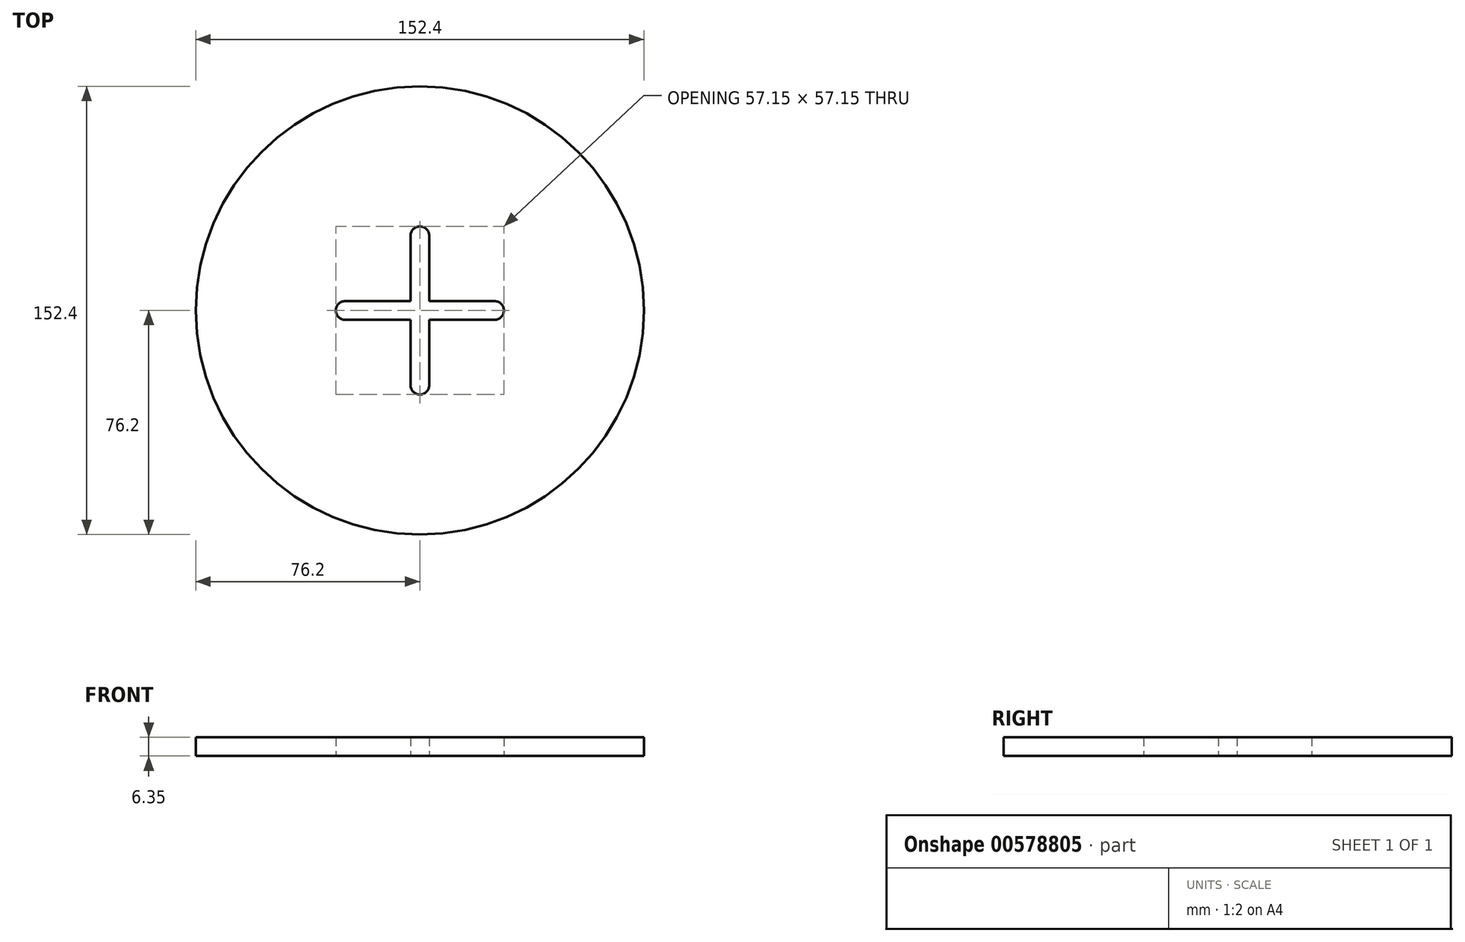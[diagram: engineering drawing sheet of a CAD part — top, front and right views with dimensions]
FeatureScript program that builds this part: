
annotation { "Feature Type Name" : "Feature", "Feature Type Description" : "" }
export const myFeature = defineFeature(function(context is Context, id is Id, definition is map)
    precondition{}
    {
        {
            var Q0;
            Q0=qCreatedBy(makeId("Top.planeOp"),FACE);
            var sketch = newSketch(context, id + "F0", { "sketchPlane" : qUnion([Q0])});
            skCircle(sketch, "E0", {"center": v(0, 0) * mm, "radius": 76.2 * mm});
            skLineSegment(sketch, "E1", {"start": v(-3.17, -3.17) * mm, "end": v(-25.4, -3.18) * mm});
            skLineSegment(sketch, "E2", {"start": v(-25.4, 3.17) * mm, "end": v(-3.17, 3.18) * mm});
            skArc(sketch, "E3", {"start": v(-25.4, 3.18) * mm, "mid": v(-28.58, 0) * mm, "end": v(-25.4, -3.18) * mm});
            skArc(sketch, "E4.MirrorCS", {"start": v(25.4, 3.18) * mm, "mid": v(28.58, 0) * mm, "end": v(25.4, -3.17) * mm});
            skLineSegment(sketch, "E5.MirrorCS", {"start": v(25.4, 3.18) * mm, "end": v(3.18, 3.18) * mm});
            skLineSegment(sketch, "E6.MirrorCS", {"start": v(3.18, -3.17) * mm, "end": v(25.4, -3.18) * mm});
            skLineSegment(sketch, "E7.left", {"start": v(-3.17, 3.18) * mm, "end": v(-3.17, 25.4) * mm});
            skLineSegment(sketch, "E7.right", {"start": v(3.18, 3.18) * mm, "end": v(3.18, 25.4) * mm});
            skArc(sketch, "E8", {"start": v(3.18, 25.4) * mm, "mid": v(0, 28.58) * mm, "end": v(-3.18, 25.4) * mm});
            skLineSegment(sketch, "E9.MirrorCS", {"start": v(-3.17, -3.17) * mm, "end": v(-3.17, -25.4) * mm});
            skLineSegment(sketch, "E10.MirrorCS", {"start": v(3.18, -3.17) * mm, "end": v(3.18, -25.4) * mm});
            skArc(sketch, "E11.MirrorCS", {"start": v(3.18, -25.4) * mm, "mid": v(0, -28.57) * mm, "end": v(-3.18, -25.4) * mm});
            skSolve(sketch);
        }
        {
            var Q0;
            Q0=makeQuery(id+"F0.imprint","IMPRINT",FACE,{"disambiguationData":[TD([[makeQuery(id+"F0.imprint","IMPRINT",EDGE,{"derivedFrom":sQuery(id+"F0.wireOp",EDGE,"E0")}),1.0]])]});
            extrude(context, id + "F1", {"entities" : qUnion([Q0]), "depth" : 6.35 * mm, "offsetDistance" : 25.4 * mm});
        }
    });
